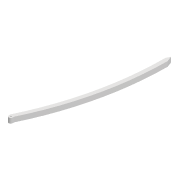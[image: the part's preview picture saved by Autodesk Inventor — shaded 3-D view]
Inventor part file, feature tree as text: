
AUTODESK INVENTOR PART (.ipt)
format: ipt  version: 2022 (Build 260153000, 153)  size: 160,256 bytes
history: native  units: mm
features: extrude x4, sketch x4, projected_geometry x3, pattern_circular x1
ambient origin geometry x8: Origin, YZ Plane, XZ Plane, XY Plane, X Axis, Y Axis, Z Axis, Center Point
bodies: Solid1 (feature_tree)
feature tree (12):
  extrude  "Extrusion1"  Depth=8.0mm
  extrude  "Extrusion5"  Depth=3.0mm
  extrude  "Extrusion6"  Depth=600.0mm
  pattern_circular  "Circular Pattern1"  Count=60  [1 undecoded]
  extrude  "Extrusion2"  Depth=8.0mm
  sketch  "Sketch1"  dims[d0=8.0mm d1=521.938mm]
  sketch  "Sketch2"  dims[d2=3.0mm d3=3.0mm]
  projected_geometry  "Projected Loop1"
  sketch  "Sketch5"  dims[d4=10.0mm d5=0.0mm d24=600.0mm d25=600.0mm]
  projected_geometry  "Projected Loop2"
  sketch  "Sketch6"  dims[d26=3.0mm d27=3.0mm d28=10.0mm d29=0.0mm d45=22.0mm d46=10.0mm d47=0.0mm d48=2.2mm d49=8.0mm d50=100.0mm d51=0.0mm d52=80.0mm d53=360.0deg d55=8.5mm]
  projected_geometry  "Projected Loop3"
note: 1 required parameter value undecoded (feature->parameter linkage not recoverable at this tier; creation-order binding heuristic only, values carry confidence <= 0.55)
